# Revit family: D100
name_source: partatom
category: Air Terminals
revit_build: Autodesk Revit 2018 (Build: 20170223_1515(x64)
units: mm (PartAtom-declared; Revit-internal decimal feet)

## family parameters
Always vertical = Yes
Cut with Voids When Loaded = No
OmniClass Number = 23.75.70.21.27.11
OmniClass Title = Diffusers, Registers, and Grilles
Part Type = Normal
Room Calculation Point = No
Round Connector Dimension = Use Diameter
Shared = No
Work Plane-Based = No

## types (2) — shared parameters
Diffuser Height = 600 mm
Diffuser Width = 600 mm
Duct Height = 300 mm
Duct Width = 300 mm
Electromagnet = Yes
Geometry = GRYFIT BX-2H, D=100 + KM, KM=150 + WT72C + EI230V, D=100. DK=140. S=6. P=190
Width 1 = 390 mm

## per-type parameters (varying)
| type | 72°C | Beginning and End (1WKKP) | Body collar width (H). | Diameter (D). | Diameter (DK). | Diameter of mounting hole (Dr). | Electromagnet type. | Electromagnet voltage. | Fire resistance class. | Length of valve (P). | Mounting frame (KM). | Value (B). | Width of gap (S). | anglXY1 | anglZ1 | diamcon1 | lengX1 | lengXY1 | lengXYZ1 | lengY1 | lengZ1 |
| 600 x 600 Face 300 x 300 Connection |  |  |  |  |  |  |  |  |  |  |  |  |  | 45.00° | 45.00° | 0 mm | 500 mm  [stored 1.64042 ft] | 2899 mm | 3100 mm | 500 mm  [stored 1.64042 ft] | 707 mm |
| GRYFIT BX-2H, D=100 + KM, KM=150 + WT72C + EI230V, D=100. DK=140. S=6. P=190 | 72°C | None | 9 | 100 | 140 | 140 | impulse | 230V AC | EIS 120 | 190 | 150 | 114 | 6 | 180.00° | 0.00° | 100 mm | 0 mm  [stored 0 ft] | 600 mm | 500 mm  [stored 1.64042 ft] | 0 mm  [stored 0 ft] | 0 mm  [stored 0 ft] |

note: [stored X ft] marks values corroborated as IEEE doubles in the binary element streams (Revit-internal decimal feet)

## geometry (parser evidence)
native form markers: Sweep x7
no freeform markers — native parametric forms only
